# Revit family: WashbasinUnit-45cm-WithDoors-Right-Vitra-ArchiPlanSeries-66556+66557+66558
name_source: partatom
category: Furniture Systems
revit_build: Autodesk Revit 2017 (Build: 20160225_1515(x64)
units: mm (PartAtom-declared; Revit-internal decimal feet)

## family parameters
Cut with Voids When Loaded = No
Host = Face
OmniClass Number = 23.40.00.00
OmniClass Title = Equipment and Furnishings
Part Type = Normal
Room Calculation Point = No
Round Connector Dimension = Use Diameter
Shared = Yes

## types (3) — shared parameters
BIMobject category = Bathroom compound units
Brand = VitrA
Default Elevation = 660 mm
Description = ArchiPlan Washbasin Unit
Design country = Turkey
IFC Classification = Furniture
Main Material = Wood
Manufacturer = Vitra
Manufacturer name = Vitra
Masterformat 2014 Code = 13 42 13
Masterformat 2014 Description = Bathroom Unit Modules
Mounting type = Wall Mounted
NBS Referans Code = 35-75-08
NBS Referans Description = Bathroom Cabinets
Nominal Depth (mm) = 375 mm
Nominal Height (mm) = 445 mm
Nominal Width (mm) = 440 mm  [stored 1.44357 ft]
OmniClass Code = 23-31 25 13
OmniClass Description = Bathroom Cabinets
Product certification = https://www.vitraglobal.com
Product family = ArchiPlan
Product group = Washbasin Unit
Product url = https://www.vitra.com.tr
Secondary Material = 153 -Oak -Thermoform
Technical description = https://www.vitra.com.tr
UNSPSC Description = Bathroom Cabinets
URL = https://vitraglobal.com
Uniclass 1.4 Code = L8241
Uniclass 1.4 Description = Bathroom Cabinets
Uniclass 2.0 Code = PR-35-75-08
Uniclass 2.0 Description = Bathroom Cabinets
Uniclass 2015 Code = Pr_40_20_93
Uniclass 2015 Name = Wash basins, sinks and troughs
Uniformat II Code = E20
Uniformat II Description = FURNISHINGS
Warranty Period (Year) = 2
Youtube = https://www.youtube.com

## per-type parameters (varying)
| type | Article No. (default) | Color | Model | Primary Material | Product SKU |
| WashbasinUnit-45cm-WithDoors-Vitra-ArchiPlanSeries-66557 | 66557 | Matte Black | 66557 | BL10 - Matte Black - Lacquered | 66557 |
| WashbasinUnit-45cm-WithDoors-Vitra-ArchiPlanSeries-66556 | 66556 | Matte White | 66556 | 117 -Matte White -Thermoform | 66556 |
| WashbasinUnit-45cm-WithDoors-Vitra-ArchiPlanSeries-66558 | 66558 | Matt Taupe | 66558 | Matt Taupe | 66558 |

note: [stored X ft] marks values corroborated as IEEE doubles in the binary element streams (Revit-internal decimal feet)

## geometry (parser evidence)
native form markers: Sweep x2
no freeform markers — native parametric forms only
